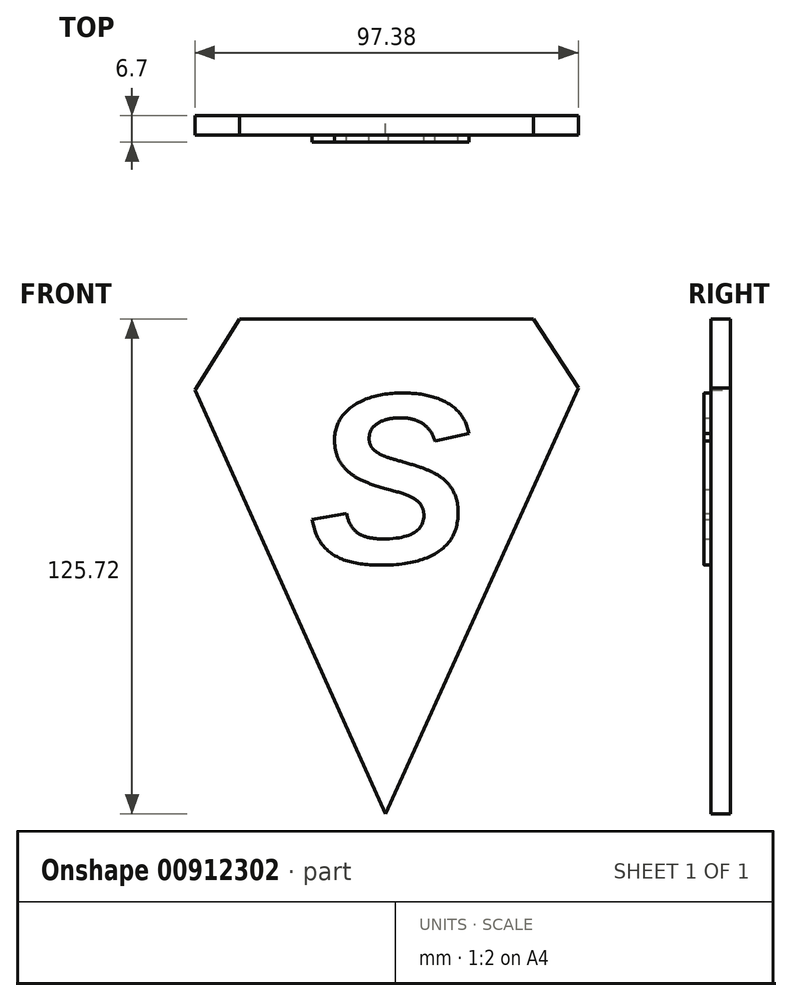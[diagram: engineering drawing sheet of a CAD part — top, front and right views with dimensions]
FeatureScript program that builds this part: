
annotation { "Feature Type Name" : "Feature", "Feature Type Description" : "" }
export const myFeature = defineFeature(function(context is Context, id is Id, definition is map)
    precondition{}
    {
        {
            var Q0;
            Q0=qCreatedBy(makeId("Front.planeOp"),FACE);
            var sketch = newSketch(context, id + "F0", { "sketchPlane" : qUnion([Q0])});
            skLineSegment(sketch, "E0", {"start": v(14.08, 49.45) * mm, "end": v(-60.58, 49.45) * mm});
            skLineSegment(sketch, "E1", {"start": v(-60.58, 49.45) * mm, "end": v(-71.94, 31.42) * mm});
            skLineSegment(sketch, "E2", {"start": v(14.08, 49.45) * mm, "end": v(25.44, 31.88) * mm});
            skLineSegment(sketch, "E3", {"start": v(-71.94, 31.42) * mm, "end": v(-23.47, -76.27) * mm});
            skLineSegment(sketch, "E4", {"start": v(25.44, 31.88) * mm, "end": v(-23.47, -76.27) * mm});
            skSolve(sketch);
        }
        {
            var Q0;
            Q0 = qSketchRegion(id + "F0", true);
            extrude(context, id + "F1", {"entities" : qUnion([Q0]), "endBound" : BoundingType.SYMMETRIC, "depth" : 5 * mm, "offsetDistance" : 25 * mm});
        }
        {
            var Q0;
            Q0=makeQuery(id+"F1.opExtrude","CAP_FACE",FACE,{"disambiguationData":[OSD([sQuery(id+"F0.wireOp",EDGE,"E0"),sQuery(id+"F0.wireOp",EDGE,"E1"),sQuery(id+"F0.wireOp",EDGE,"E2"),sQuery(id+"F0.wireOp",EDGE,"E3"),sQuery(id+"F0.wireOp",EDGE,"E4")])],"isStart":false});
            var sketch = newSketch(context, id + "F2", { "sketchPlane" : qUnion([Q0])});
            skText(sketch, "E5", { "text": "S", "fontName": "Arimo-BoldItalic.ttf"});
            const initialGuessF2  = {"E5": [-0.04288, -0.01246, 1, 0, 0.04447]};
            skSetInitialGuess(sketch, initialGuessF2);
            skSolve(sketch);
        }
        {
            var Q0;
            Q0 = qSketchRegion(id + "F2", true);
            extrude(context, id + "F3", {"entities" : qUnion([Q0]), "operationType" : NewBodyOperationType.ADD, "endBound" : BoundingType.SYMMETRIC, "depth" : 3.4 * mm, "offsetDistance" : 25 * mm});
        }
    });
